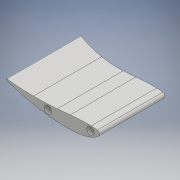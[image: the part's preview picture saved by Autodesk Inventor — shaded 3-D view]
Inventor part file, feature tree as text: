
AUTODESK INVENTOR PART (.ipt)
format: ipt  version: 2018 (Build 220112000, 112)  size: 328,192 bytes
history: native  units: mm
features: other x6, extrude x5, sketch x5, reference x4, projected_geometry x3
ambient origin geometry x8: Origin, YZ Plane, XZ Plane, XY Plane, X Axis, Y Axis, Z Axis, Center Point
bodies: Body1 (feature_tree)
feature tree (23):
  extrude  "押し出し1"  Depth=250.0mm TaperAngle=0.0deg
  other  "作業平面1"
  extrude  "押し出し4"  Depth=225.0mm TaperAngle=0.0deg
  extrude  "押し出し5"  Depth=10.0mm TaperAngle=0.0deg
  extrude  "押し出し6"  Depth=10.0mm TaperAngle=0.0deg
  extrude  "押し出し7"  Depth=41.667mm
  sketch  "スケッチ1"
  projected_geometry  "投影ループ1"
  sketch  "スケッチ4"
  reference  "参照3"
  reference  "参照4"
  sketch  "スケッチ5"
  projected_geometry  "投影ループ2"
  sketch  "スケッチ6"
  reference  "参照5"
  reference  "参照6"
  sketch  "スケッチ7"
  projected_geometry  "投影ループ3"
  other  "<userpath>\Documents\Inventor\Aero\KS-15\Fr.wing\Fr.wing_assy.iam"
  other  "Fr.wing_assy.iam"
  other  "endplate_ver2:2"
  other  "Part1:1"
  other  "newbracket2:1"
